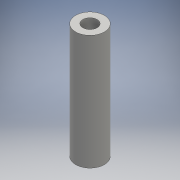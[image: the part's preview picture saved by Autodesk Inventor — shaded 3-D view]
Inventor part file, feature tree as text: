
AUTODESK INVENTOR PART (.ipt)
format: ipt  version: 2016 (Build 200138000, 138)  size: 91,648 bytes
history: native  units: mm
features: other x1, extrude x1, sketch x1
ambient origin geometry x8: Origin, YZ Plane, XZ Plane, XY Plane, X Axis, Y Axis, Z Axis, Center Point
bodies: Body1 (feature_tree)
feature tree (3):
  other  "ソリッド1"
  extrude  "押し出し1"  Depth=8.0mm
  sketch  "スケッチ1"
